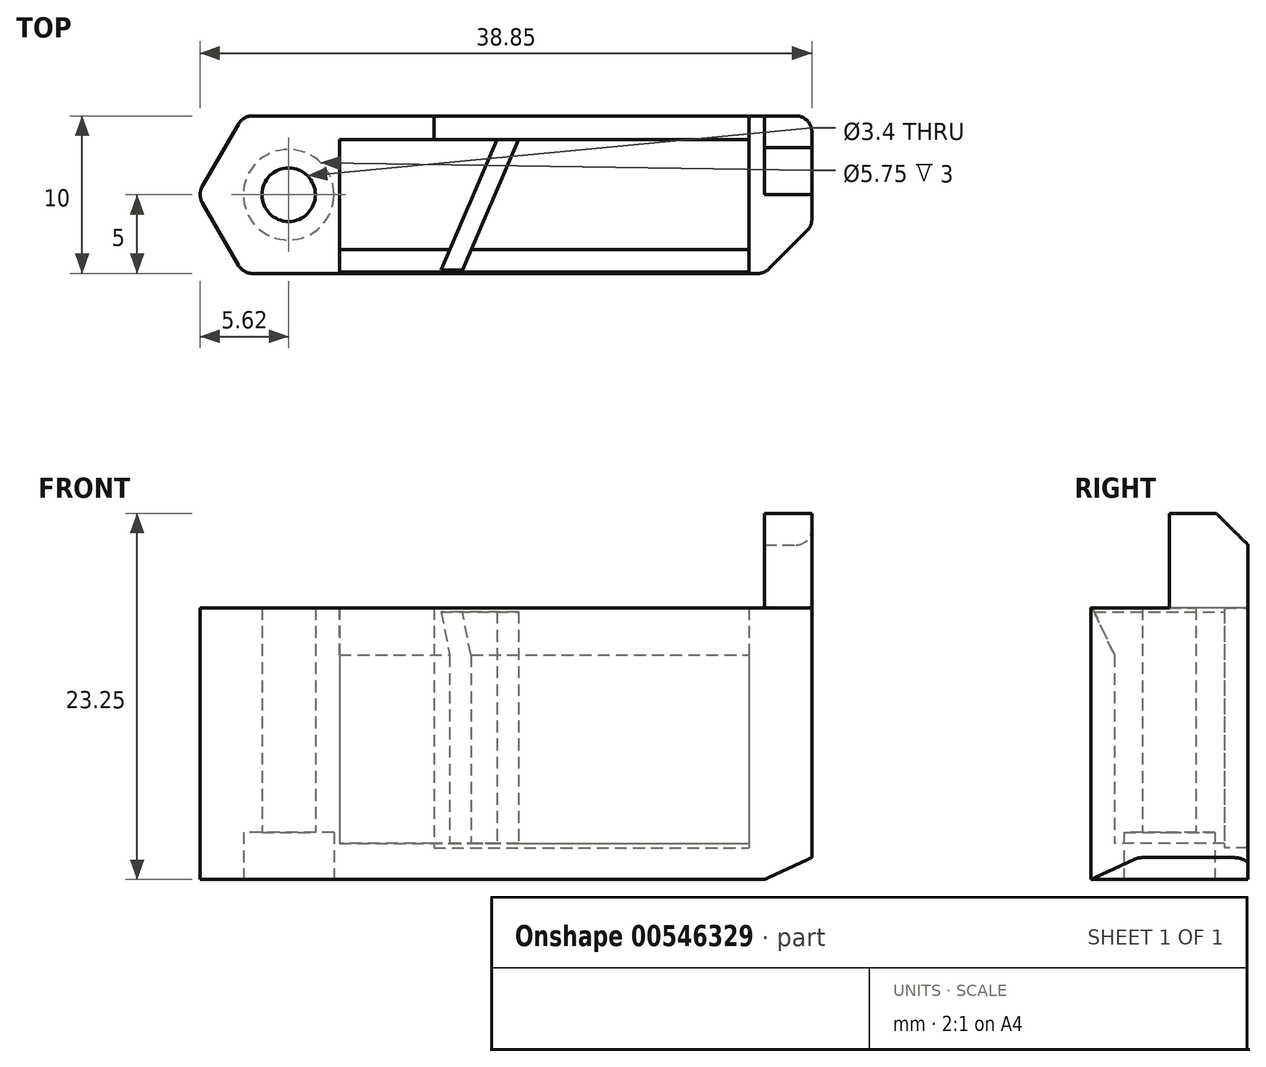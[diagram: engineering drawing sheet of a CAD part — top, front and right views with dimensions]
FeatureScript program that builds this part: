
annotation { "Feature Type Name" : "Feature", "Feature Type Description" : "" }
export const myFeature = defineFeature(function(context is Context, id is Id, definition is map)
    precondition{}
    {
        {
            var Q0;
            Q0=qCreatedBy(makeId("Top.planeOp"),FACE);
            var sketch = newSketch(context, id + "F0", { "sketchPlane" : qUnion([Q0])});
            skLineSegment(sketch, "E0.bottom", {"start": v(-5.77, 5) * mm, "end": v(33.23, 5) * mm});
            skLineSegment(sketch, "E0.top", {"start": v(-5.77, -5) * mm, "end": v(33.23, -5) * mm});
            skLineSegment(sketch, "E0.left", {"start": v(-5.77, 5) * mm, "end": v(-5.77, -5) * mm});
            skLineSegment(sketch, "E0.right", {"start": v(33.23, 5) * mm, "end": v(33.23, -5) * mm});
            skCircle(sketch, "E1", {"center": v(0, 0) * mm, "radius": 2.88 * mm});
            skSolve(sketch);
        }
        {
            var Q0;
            Q0=makeQuery(id+"F0.imprint","IMPRINT",FACE,{"disambiguationData":[TD([[makeQuery(id+"F0.imprint","IMPRINT",EDGE,{"derivedFrom":sQuery(id+"F0.wireOp",EDGE,"E0.top")}),1.0]])]});
            var Q1;
            Q1=makeQuery(id+"F0.imprint","IMPRINT",FACE,{"disambiguationData":[TD([[makeQuery(id+"F0.imprint","IMPRINT",EDGE,{"derivedFrom":sQuery(id+"F0.wireOp",EDGE,"7lKz8HTh-Vj5R-iSY0-jH6W-7n2KpUGulIUN.bottom")}),-1.0]])]});
            var Q2;
            Q2=makeQuery(id+"F0.imprint","IMPRINT",FACE,{"disambiguationData":[TD([[makeQuery(id+"F0.imprint","IMPRINT",EDGE,{"derivedFrom":sQuery(id+"F0.wireOp",EDGE,"X53WlA5K-zrl0-lVQD-ScPo-aY7akJ4aOTbb.bottom")}),1.0]])]});
            extrude(context, id + "F1", {"entities" : qUnion([Q0, Q1, Q2]), "depth" : 2 * mm, "offsetDistance" : 25 * mm});
        }
        {
            var Q0;
            Q0=makeQuery(id+"F1.opExtrude","CAP_FACE",FACE,{"disambiguationData":[OSD([sQuery(id+"F0.wireOp",EDGE,"E0.bottom"),sQuery(id+"F0.wireOp",EDGE,"E0.top"),sQuery(id+"F0.wireOp",EDGE,"E0.left"),sQuery(id+"F0.wireOp",EDGE,"E0.right"),sQuery(id+"F0.wireOp",EDGE,"ZELiG0B9-lqbG-wd7r-yNXl-9H2IX8axxHvB"),sQuery(id+"F0.wireOp",EDGE,"7lKz8HTh-Vj5R-iSY0-jH6W-7n2KpUGulIUN.bottom"),sQuery(id+"F0.wireOp",EDGE,"X53WlA5K-zrl0-lVQD-ScPo-aY7akJ4aOTbb.top")])],"isStart":false});
            var sketch = newSketch(context, id + "F2", { "sketchPlane" : qUnion([Q0])});
            skPoint(sketch, "E2.centerSnap0", {"position": v(-49.5, -42.6) * mm});
            skLineSegment(sketch, "E3.bottom", {"start": v(3.23, 5) * mm, "end": v(29.23, 5) * mm});
            skLineSegment(sketch, "E3.top", {"start": v(3.23, -3.5) * mm, "end": v(29.23, -3.5) * mm});
            skLineSegment(sketch, "E3.left", {"start": v(3.23, 5) * mm, "end": v(3.23, -3.5) * mm});
            skLineSegment(sketch, "E3.right", {"start": v(29.23, 5) * mm, "end": v(29.23, -3.5) * mm});
            skLineSegment(sketch, "E4.bottom", {"start": v(3.23, 3.5) * mm, "end": v(9.23, 3.5) * mm});
            skLineSegment(sketch, "E4.top", {"start": v(3.23, 5) * mm, "end": v(9.23, 5) * mm});
            skLineSegment(sketch, "E4.left", {"start": v(3.23, 3.5) * mm, "end": v(3.23, 5) * mm});
            skLineSegment(sketch, "E4.right", {"start": v(9.23, 3.5) * mm, "end": v(9.23, 5) * mm});
            skCircle(sketch, "E5", {"center": v(0, 0) * mm, "radius": 1.7 * mm});
            skSolve(sketch);
        }
        {
            var Q0;
            {var subQ12=sQuery(id+"F2.wireOp",EDGE,"E3.top");Q0=makeQuery(id+"F2.imprint","IMPRINT",FACE,{"disambiguationData":[TD([[makeQuery(id+"F2.imprint","IMPRINT",EDGE,{"derivedFrom":subQ12}),-1.0]])]});}
            var Q1;
            {var subQ0=sQuery(id+"F2.wireOp",EDGE,"E4.bottom");Q1=makeQuery(id+"F2.imprint","IMPRINT",FACE,{"disambiguationData":[TD([[makeQuery(id+"F2.imprint","IMPRINT",EDGE,{"derivedFrom":subQ0}),1.0]])]});}
            var Q2;
            Q2=makeQuery(id+"F2.imprint","IMPRINT",FACE,{"disambiguationData":[TD([[makeQuery(id+"F2.imprint","IMPRINT",EDGE,{"derivedFrom":sQuery(id+"F2.wireOp",EDGE,"E5")}),-1.0]])]});
            extrude(context, id + "F3", {"entities" : qUnion([Q0, Q1, Q2]), "operationType" : NewBodyOperationType.ADD, "depth" : 15.25 * mm, "offsetDistance" : 25 * mm});
        }
        {
            var Q0;
            Q0=makeQuery(id+"F3.opExtrude","CAP_FACE",FACE,{"disambiguationData":[OSD([sQuery(id+"F0.wireOp",EDGE,"E0.bottom"),sQuery(id+"F0.wireOp",EDGE,"E0.top"),sQuery(id+"F0.wireOp",EDGE,"E0.left"),sQuery(id+"F0.wireOp",EDGE,"E0.right"),sQuery(id+"F0.wireOp",EDGE,"7lKz8HTh-Vj5R-iSY0-jH6W-7n2KpUGulIUN.bottom"),sQuery(id+"F0.wireOp",EDGE,"X53WlA5K-zrl0-lVQD-ScPo-aY7akJ4aOTbb.top"),sQuery(id+"F2.wireOp",EDGE,"E2"),sQuery(id+"F2.wireOp",EDGE,"E3.top"),sQuery(id+"F2.wireOp",EDGE,"E3.left"),sQuery(id+"F2.wireOp",EDGE,"E3.right"),sQuery(id+"F2.wireOp",EDGE,"E4.bottom"),sQuery(id+"F2.wireOp",EDGE,"E4.top"),sQuery(id+"F2.wireOp",EDGE,"E4.right")])],"isStart":false});
            var sketch = newSketch(context, id + "F4", { "sketchPlane" : qUnion([Q0])});
            skLineSegment(sketch, "E6.bottom", {"start": v(30.23, 5) * mm, "end": v(33.23, 5) * mm});
            skLineSegment(sketch, "E6.top", {"start": v(30.23, 0) * mm, "end": v(33.23, 0) * mm});
            skLineSegment(sketch, "E6.left", {"start": v(30.23, 5) * mm, "end": v(30.23, 0) * mm});
            skLineSegment(sketch, "E6.right", {"start": v(33.23, 5) * mm, "end": v(33.23, 0) * mm});
            skSolve(sketch);
        }
        {
            var Q0;
            Q0=makeQuery(id+"F4.imprint","IMPRINT",FACE,{"disambiguationData":[TD([[makeQuery(id+"F4.imprint","IMPRINT",EDGE,{"derivedFrom":sQuery(id+"F4.wireOp",EDGE,"E6.bottom")}),-1.0]])]});
            extrude(context, id + "F5", {"entities" : qUnion([Q0]), "operationType" : NewBodyOperationType.ADD, "depth" : 6 * mm, "offsetDistance" : 25 * mm});
        }
        {
            var Q0;
            Q0=makeQuery(id+"F3.boolean.opBoolean","MERGE",EDGE,{"derivedFrom":[makeQuery(id+"F1.opExtrude","SWEPT_EDGE",EDGE,{"disambiguationData":[OSD([sQuery(id+"F0.wireOp",EDGE,"E0.bottom"),sQuery(id+"F0.wireOp",EDGE,"E0.left")])]}),makeQuery(id+"F3.opExtrude","SWEPT_EDGE",EDGE,{"disambiguationData":[OSD([sQuery(id+"F2.wireOp",EDGE,"13d9e1a8-76b6-46fc-9b6f-012af6129c84.bottom"),sQuery(id+"F2.wireOp",EDGE,"13d9e1a8-76b6-46fc-9b6f-012af6129c84.left")])]})]});
            var Q1;
            Q1=makeQuery(id+"F3.boolean.opBoolean","MERGE",EDGE,{"derivedFrom":[makeQuery(id+"F1.opExtrude","SWEPT_EDGE",EDGE,{"disambiguationData":[OSD([sQuery(id+"F0.wireOp",EDGE,"E0.top"),sQuery(id+"F0.wireOp",EDGE,"E0.left")])]}),makeQuery(id+"F3.opExtrude","SWEPT_EDGE",EDGE,{"disambiguationData":[OSD([sQuery(id+"F2.wireOp",EDGE,"13d9e1a8-76b6-46fc-9b6f-012af6129c84.top"),sQuery(id+"F2.wireOp",EDGE,"13d9e1a8-76b6-46fc-9b6f-012af6129c84.left")])]})]});
            chamfer(context, id + "F6", {"entities" : qUnion([Q0, Q1]), "chamferType" : ChamferType.OFFSET_ANGLE, "width" : 5 * mm, "oppositeDirection" : false, "angle" : 30 * degree, "tangentPropagation" : true});
        }
        {
            var Q0;
            Q0=makeQuery(id+"F3.boolean.opBoolean","MERGE",EDGE,{"derivedFrom":[makeQuery(id+"F1.opExtrude","SWEPT_EDGE",EDGE,{"disambiguationData":[OSD([sQuery(id+"F0.wireOp",EDGE,"E0.top"),sQuery(id+"F0.wireOp",EDGE,"E0.right")])]}),makeQuery(id+"F3.opExtrude","SWEPT_EDGE",EDGE,{"disambiguationData":[OSD([sQuery(id+"F2.wireOp",EDGE,"13d9e1a8-76b6-46fc-9b6f-012af6129c84.top"),sQuery(id+"F2.wireOp",EDGE,"13d9e1a8-76b6-46fc-9b6f-012af6129c84.right")])]})]});
            chamfer(context, id + "F7", {"entities" : qUnion([Q0]), "chamferType" : ChamferType.OFFSET_ANGLE, "width" : 3 * mm, "oppositeDirection" : false, "angle" : 45 * degree, "tangentPropagation" : true});
        }
        {
            var Q0;
            Q0=makeQuery(id+"F1.opExtrude","CAP_FACE",FACE,{"disambiguationData":[OSD([sQuery(id+"F0.wireOp",EDGE,"E0.bottom"),sQuery(id+"F0.wireOp",EDGE,"E0.top"),sQuery(id+"F0.wireOp",EDGE,"E0.left"),sQuery(id+"F0.wireOp",EDGE,"E0.right"),sQuery(id+"F0.wireOp",EDGE,"ZELiG0B9-lqbG-wd7r-yNXl-9H2IX8axxHvB"),sQuery(id+"F0.wireOp",EDGE,"7lKz8HTh-Vj5R-iSY0-jH6W-7n2KpUGulIUN.bottom"),sQuery(id+"F0.wireOp",EDGE,"X53WlA5K-zrl0-lVQD-ScPo-aY7akJ4aOTbb.top")])],"isStart":true});
            var sketch = newSketch(context, id + "F8", { "sketchPlane" : qUnion([Q0])});
            skSolve(sketch);
        }
        {
            var Q0;
            Q0=makeQuery(id+"F8.imprint","IMPRINT",FACE,{"disambiguationData":[TD([[makeQuery(id+"F8.imprint","IMPRINT",EDGE,{"derivedFrom":makeQuery(id+"F1.opExtrude","CAP_EDGE",EDGE,{"disambiguationData":[OSD([sQuery(id+"F0.wireOp",EDGE,"E1")])],"isStart":true})}),-1.0]])]});
            extrude(context, id + "F9", {"entities" : qUnion([Q0]), "operationType" : NewBodyOperationType.REMOVE, "oppositeDirection" : true, "depth" : 3 * mm, "offsetDistance" : 25 * mm});
        }
        {
            var Q0;
            Q0=makeQuery(id+"F5.opExtrude","CAP_EDGE",EDGE,{"disambiguationData":[OSD([sQuery(id+"F4.wireOp",EDGE,"E6.bottom")])],"isStart":false});
            chamfer(context, id + "F10", {"entities" : qUnion([Q0]), "width" : 2 * mm, "tangentPropagation" : true});
        }
        {
            var Q0;
            Q0=makeQuery(id+"F1.opExtrude","CAP_FACE",FACE,{"disambiguationData":[OSD([sQuery(id+"F0.wireOp",EDGE,"E0.bottom"),sQuery(id+"F0.wireOp",EDGE,"E0.top"),sQuery(id+"F0.wireOp",EDGE,"E0.left"),sQuery(id+"F0.wireOp",EDGE,"E0.right"),sQuery(id+"F0.wireOp",EDGE,"ZELiG0B9-lqbG-wd7r-yNXl-9H2IX8axxHvB"),sQuery(id+"F0.wireOp",EDGE,"7lKz8HTh-Vj5R-iSY0-jH6W-7n2KpUGulIUN.bottom"),sQuery(id+"F0.wireOp",EDGE,"X53WlA5K-zrl0-lVQD-ScPo-aY7akJ4aOTbb.top")])],"isStart":false});
            var sketch = newSketch(context, id + "F11", { "sketchPlane" : qUnion([Q0])});
            skLineSegment(sketch, "E7", {"start": v(10.23, -3.5) * mm, "end": v(13.23, 3.5) * mm});
            skLineSegment(sketch, "E8", {"start": v(13.23, 3.5) * mm, "end": v(14.59, 3.5) * mm});
            skLineSegment(sketch, "E9", {"start": v(14.59, 3.5) * mm, "end": v(11.59, -3.5) * mm});
            skLineSegment(sketch, "E10", {"start": v(13.23, 3.5) * mm, "end": v(3.23, 3.5) * mm});
            skLineSegment(sketch, "E11", {"start": v(14.59, 3.5) * mm, "end": v(29.23, 3.5) * mm});
            skSolve(sketch);
        }
        {
            var Q0;
            {var subQ0=sQuery(id+"F11.wireOp",EDGE,"E7");Q0=makeQuery(id+"F11.imprint","IMPRINT",FACE,{"disambiguationData":[TD([[makeQuery(id+"F11.imprint","IMPRINT",EDGE,{"derivedFrom":subQ0}),-1.0]])]});}
            extrude(context, id + "F12", {"entities" : qUnion([Q0]), "operationType" : NewBodyOperationType.ADD, "depth" : 15 * mm, "offsetDistance" : 25 * mm});
        }
        {
            var Q0;
            Q0=makeQuery(id+"F3.opExtrude","CAP_EDGE",EDGE,{"disambiguationData":[OSD([sQuery(id+"F2.wireOp",EDGE,"E3.top")])],"isStart":false});
            var Q1;
            Q1=makeQuery(id+"F1.opExtrude","CAP_EDGE",EDGE,{"disambiguationData":[OSD([sQuery(id+"F0.wireOp",EDGE,"E0.right")])],"isStart":true});
            chamfer(context, id + "F13", {"entities" : qUnion([Q0, Q1]), "chamferType" : ChamferType.OFFSET_ANGLE, "width" : 3 * mm, "oppositeDirection" : false, "angle" : 25 * degree, "tangentPropagation" : true});
        }
        {
            var Q0;
            {var subQ0=sQuery(id+"F0.wireOp",EDGE,"E0.right");var subQ1=sQuery(id+"F0.wireOp",EDGE,"E0.bottom");Q0=makeQuery(id+"F5.boolean.opBoolean","MERGE",EDGE,{"derivedFrom":[makeQuery(id+"F3.boolean.opBoolean","MERGE",EDGE,{"derivedFrom":[makeQuery(id+"F1.opExtrude","SWEPT_EDGE",EDGE,{"disambiguationData":[OSD([subQ1,subQ0])]}),makeQuery(id+"F3.opExtrude","SWEPT_EDGE",EDGE,{"disambiguationData":[OSD([subQ1,subQ0,sQuery(id+"F0.wireOp",EDGE,"7lKz8HTh-Vj5R-iSY0-jH6W-7n2KpUGulIUN.bottom"),sQuery(id+"F0.wireOp",EDGE,"X53WlA5K-zrl0-lVQD-ScPo-aY7akJ4aOTbb.top")])]})]}),makeQuery(id+"F5.opExtrude","SWEPT_EDGE",EDGE,{"disambiguationData":[OSD([sQuery(id+"F4.wireOp",EDGE,"E6.bottom"),sQuery(id+"F4.wireOp",EDGE,"E6.right")])]})]});}
            var Q1;
            {var subQ0=sQuery(id+"F0.wireOp",EDGE,"X53WlA5K-zrl0-lVQD-ScPo-aY7akJ4aOTbb.top");var subQ1=sQuery(id+"F0.wireOp",EDGE,"7lKz8HTh-Vj5R-iSY0-jH6W-7n2KpUGulIUN.bottom");var subQ2=sQuery(id+"F0.wireOp",EDGE,"E0.bottom");var subQ3=sQuery(id+"F0.wireOp",EDGE,"E0.left");Q1=makeQuery(id+"F6.opChamfer","BLEND_EDGE",EDGE,{"blendedFrom":[makeQuery(id+"F3.boolean.opBoolean","MERGE",EDGE,{"derivedFrom":[makeQuery(id+"F1.opExtrude","SWEPT_EDGE",EDGE,{"disambiguationData":[OSD([subQ2,subQ3])]}),makeQuery(id+"F3.opExtrude","SWEPT_EDGE",EDGE,{"disambiguationData":[OSD([subQ2,subQ3,subQ1,subQ0])]})]}),makeQuery(id+"F5.boolean.opBoolean","MERGE",FACE,{"derivedFrom":[makeQuery(id+"F3.boolean.opBoolean","MERGE",FACE,{"derivedFrom":[makeQuery(id+"F1.opExtrude","SWEPT_FACE",FACE,{"disambiguationData":[OSD([subQ2,subQ1,subQ0])]}),makeQuery(id+"F3.opExtrude","SWEPT_FACE",FACE,{"disambiguationData":[OSD([subQ2,subQ1,subQ0,sQuery(id+"F2.wireOp",EDGE,"E4.top")])]}),makeQuery(id+"F3.opExtrude","SWEPT_FACE",FACE,{"disambiguationData":[OSD([subQ2,subQ1,subQ0])]})]}),makeQuery(id+"F5.opExtrude","SWEPT_FACE",FACE,{"disambiguationData":[OSD([sQuery(id+"F4.wireOp",EDGE,"E6.bottom")])]})]})],"blendedInto":[makeQuery(id+"F5.boolean.opBoolean","MERGE",FACE,{"derivedFrom":[makeQuery(id+"F3.boolean.opBoolean","MERGE",FACE,{"derivedFrom":[makeQuery(id+"F1.opExtrude","SWEPT_FACE",FACE,{"disambiguationData":[OSD([subQ2,subQ1,subQ0])]}),makeQuery(id+"F3.opExtrude","SWEPT_FACE",FACE,{"disambiguationData":[OSD([subQ2,subQ1,subQ0,sQuery(id+"F2.wireOp",EDGE,"E4.top")])]}),makeQuery(id+"F3.opExtrude","SWEPT_FACE",FACE,{"disambiguationData":[OSD([subQ2,subQ1,subQ0])]})]}),makeQuery(id+"F5.opExtrude","SWEPT_FACE",FACE,{"disambiguationData":[OSD([sQuery(id+"F4.wireOp",EDGE,"E6.bottom")])]})]})]});}
            var Q2;
            {var subQ0=sQuery(id+"F0.wireOp",EDGE,"E0.left");var subQ1=sQuery(id+"F0.wireOp",EDGE,"E0.top");var subQ2=sQuery(id+"F0.wireOp",EDGE,"E0.bottom");Q2=makeQuery(id+"F6.opChamfer","BLEND_EDGE",EDGE,{"blendedFrom":[makeQuery(id+"F3.boolean.opBoolean","MERGE",EDGE,{"derivedFrom":[makeQuery(id+"F1.opExtrude","SWEPT_EDGE",EDGE,{"disambiguationData":[OSD([subQ2,subQ0])]}),makeQuery(id+"F3.opExtrude","SWEPT_EDGE",EDGE,{"disambiguationData":[OSD([subQ2,subQ0,sQuery(id+"F0.wireOp",EDGE,"7lKz8HTh-Vj5R-iSY0-jH6W-7n2KpUGulIUN.bottom"),sQuery(id+"F0.wireOp",EDGE,"X53WlA5K-zrl0-lVQD-ScPo-aY7akJ4aOTbb.top")])]})]}),makeQuery(id+"F3.boolean.opBoolean","MERGE",EDGE,{"derivedFrom":[makeQuery(id+"F1.opExtrude","SWEPT_EDGE",EDGE,{"disambiguationData":[OSD([subQ1,subQ0])]}),makeQuery(id+"F3.opExtrude","SWEPT_EDGE",EDGE,{"disambiguationData":[OSD([subQ1,subQ0])]})]})],"blendedInto":[]});}
            var Q3;
            {var subQ0=sQuery(id+"F0.wireOp",EDGE,"E0.top");var subQ1=sQuery(id+"F0.wireOp",EDGE,"E0.left");Q3=makeQuery(id+"F6.opChamfer","BLEND_EDGE",EDGE,{"blendedFrom":[makeQuery(id+"F3.boolean.opBoolean","MERGE",EDGE,{"derivedFrom":[makeQuery(id+"F1.opExtrude","SWEPT_EDGE",EDGE,{"disambiguationData":[OSD([subQ0,subQ1])]}),makeQuery(id+"F3.opExtrude","SWEPT_EDGE",EDGE,{"disambiguationData":[OSD([subQ0,subQ1])]})]}),makeQuery(id+"F3.boolean.opBoolean","MERGE",FACE,{"derivedFrom":[makeQuery(id+"F1.opExtrude","SWEPT_FACE",FACE,{"disambiguationData":[OSD([subQ0])]}),makeQuery(id+"F3.opExtrude","SWEPT_FACE",FACE,{"disambiguationData":[OSD([subQ0])]})]})],"blendedInto":[makeQuery(id+"F3.boolean.opBoolean","MERGE",FACE,{"derivedFrom":[makeQuery(id+"F1.opExtrude","SWEPT_FACE",FACE,{"disambiguationData":[OSD([subQ0])]}),makeQuery(id+"F3.opExtrude","SWEPT_FACE",FACE,{"disambiguationData":[OSD([subQ0])]})]})]});}
            var Q4;
            {var subQ0=sQuery(id+"F0.wireOp",EDGE,"E0.right");var subQ1=sQuery(id+"F0.wireOp",EDGE,"E0.top");Q4=makeQuery(id+"F7.opChamfer","BLEND_EDGE",EDGE,{"blendedFrom":[makeQuery(id+"F3.boolean.opBoolean","MERGE",EDGE,{"derivedFrom":[makeQuery(id+"F1.opExtrude","SWEPT_EDGE",EDGE,{"disambiguationData":[OSD([subQ1,subQ0])]}),makeQuery(id+"F3.opExtrude","SWEPT_EDGE",EDGE,{"disambiguationData":[OSD([subQ1,subQ0])]})]}),makeQuery(id+"F5.boolean.opBoolean","MERGE",FACE,{"derivedFrom":[makeQuery(id+"F3.boolean.opBoolean","MERGE",FACE,{"derivedFrom":[makeQuery(id+"F1.opExtrude","SWEPT_FACE",FACE,{"disambiguationData":[OSD([subQ0])]}),makeQuery(id+"F3.opExtrude","SWEPT_FACE",FACE,{"disambiguationData":[OSD([subQ0])]})]}),makeQuery(id+"F5.opExtrude","SWEPT_FACE",FACE,{"disambiguationData":[OSD([sQuery(id+"F4.wireOp",EDGE,"E6.right")])]})]})],"blendedInto":[makeQuery(id+"F5.boolean.opBoolean","MERGE",FACE,{"derivedFrom":[makeQuery(id+"F3.boolean.opBoolean","MERGE",FACE,{"derivedFrom":[makeQuery(id+"F1.opExtrude","SWEPT_FACE",FACE,{"disambiguationData":[OSD([subQ0])]}),makeQuery(id+"F3.opExtrude","SWEPT_FACE",FACE,{"disambiguationData":[OSD([subQ0])]})]}),makeQuery(id+"F5.opExtrude","SWEPT_FACE",FACE,{"disambiguationData":[OSD([sQuery(id+"F4.wireOp",EDGE,"E6.right")])]})]})]});}
            var Q5;
            {var subQ0=sQuery(id+"F0.wireOp",EDGE,"E0.top");var subQ1=sQuery(id+"F0.wireOp",EDGE,"E0.right");Q5=makeQuery(id+"F7.opChamfer","BLEND_EDGE",EDGE,{"blendedFrom":[makeQuery(id+"F3.boolean.opBoolean","MERGE",EDGE,{"derivedFrom":[makeQuery(id+"F1.opExtrude","SWEPT_EDGE",EDGE,{"disambiguationData":[OSD([subQ0,subQ1])]}),makeQuery(id+"F3.opExtrude","SWEPT_EDGE",EDGE,{"disambiguationData":[OSD([subQ0,subQ1])]})]}),makeQuery(id+"F3.boolean.opBoolean","MERGE",FACE,{"derivedFrom":[makeQuery(id+"F1.opExtrude","SWEPT_FACE",FACE,{"disambiguationData":[OSD([subQ0])]}),makeQuery(id+"F3.opExtrude","SWEPT_FACE",FACE,{"disambiguationData":[OSD([subQ0])]})]})],"blendedInto":[makeQuery(id+"F3.boolean.opBoolean","MERGE",FACE,{"derivedFrom":[makeQuery(id+"F1.opExtrude","SWEPT_FACE",FACE,{"disambiguationData":[OSD([subQ0])]}),makeQuery(id+"F3.opExtrude","SWEPT_FACE",FACE,{"disambiguationData":[OSD([subQ0])]})]})]});}
            fillet(context, id + "F14", {"entities" : qUnion([Q0, Q1, Q2, Q3, Q4, Q5]), "radius" : 1 * mm, "tangentPropagation" : true, "allowEdgeOverflow" : false});
        }
        {
            var Q0;
            {var subQ0=sQuery(id+"F11.wireOp",EDGE,"E7");Q0=makeQuery(id+"F11.imprint","IMPRINT",FACE,{"disambiguationData":[TD([[makeQuery(id+"F11.imprint","IMPRINT",EDGE,{"derivedFrom":subQ0}),1.0]])]});}
            var Q1;
            {var subQ0=sQuery(id+"F11.wireOp",EDGE,"E9");Q1=makeQuery(id+"F11.imprint","IMPRINT",FACE,{"disambiguationData":[TD([[makeQuery(id+"F11.imprint","IMPRINT",EDGE,{"derivedFrom":subQ0}),1.0]])]});}
            extrude(context, id + "F15", {"entities" : qUnion([Q0, Q1]), "operationType" : NewBodyOperationType.ADD, "depth" : 0.3 * mm, "offsetDistance" : 25 * mm});
        }
    });
